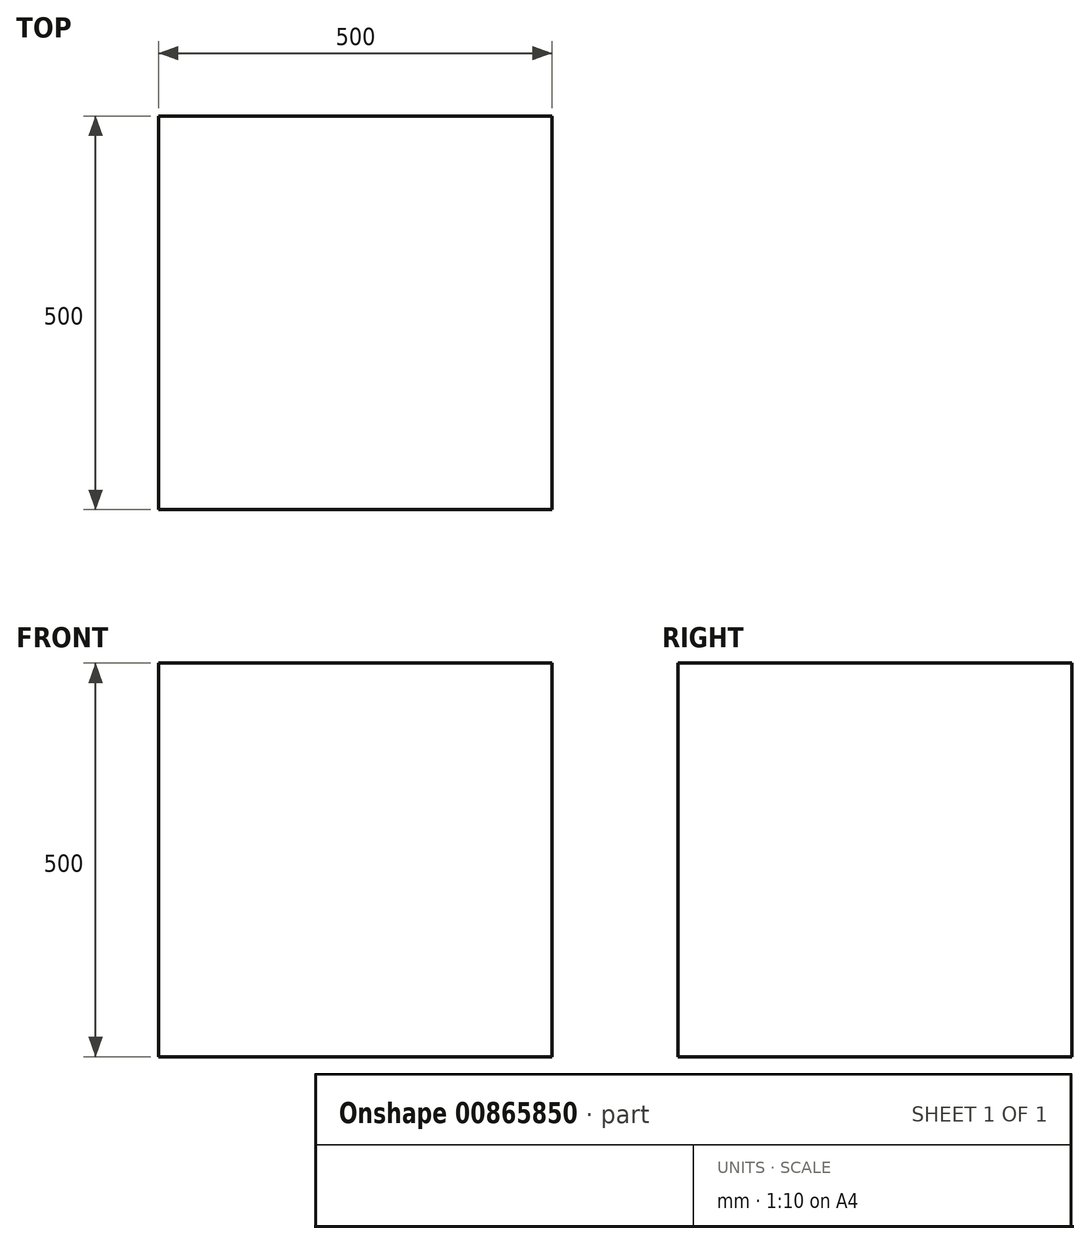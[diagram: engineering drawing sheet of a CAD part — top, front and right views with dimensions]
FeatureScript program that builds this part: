
annotation { "Feature Type Name" : "Feature", "Feature Type Description" : "" }
export const myFeature = defineFeature(function(context is Context, id is Id, definition is map)
    precondition{}
    {
        {
            var Q0;
            Q0=qCreatedBy(makeId("Top.planeOp"),FACE);
            var sketch = newSketch(context, id + "F0", { "sketchPlane" : qUnion([Q0])});
            skLineSegment(sketch, "E0.bottom", {"start": v(-250, 250) * mm, "end": v(250, 250) * mm});
            skLineSegment(sketch, "E0.top", {"start": v(-250, -250) * mm, "end": v(250, -250) * mm});
            skLineSegment(sketch, "E0.left", {"start": v(-250, 250) * mm, "end": v(-250, -250) * mm});
            skLineSegment(sketch, "E0.right", {"start": v(250, 250) * mm, "end": v(250, -250) * mm});
            skPoint(sketch, "E0.middle", {"position": v(0, 0) * mm});
            skSolve(sketch);
        }
        {
            var Q0;
            Q0 = qSketchRegion(id + "F0", true);
            extrude(context, id + "F1", {"entities" : qUnion([Q0]), "depth" : 500 * mm, "offsetDistance" : 25 * mm});
        }
    });
